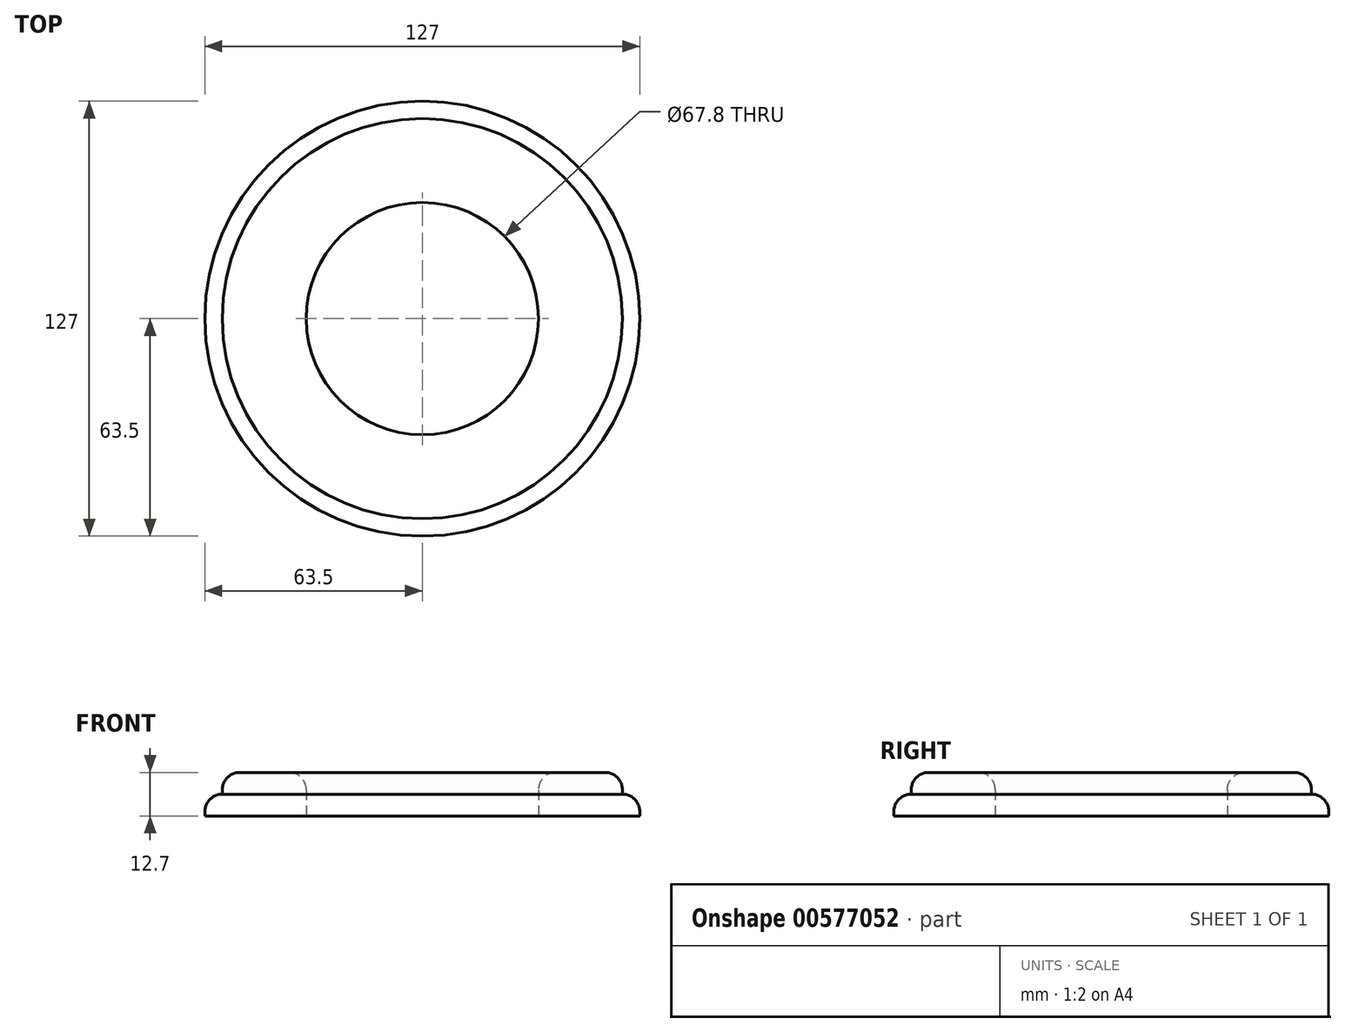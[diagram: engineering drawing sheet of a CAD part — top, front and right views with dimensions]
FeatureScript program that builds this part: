
annotation { "Feature Type Name" : "Feature", "Feature Type Description" : "" }
export const myFeature = defineFeature(function(context is Context, id is Id, definition is map)
    precondition{}
    {
        {
            var Q0;
            Q0=qCreatedBy(makeId("Top.planeOp"),FACE);
            var sketch = newSketch(context, id + "F0", { "sketchPlane" : qUnion([Q0])});
            skCircle(sketch, "E0", {"center": v(0, 0) * mm, "radius": 63.5 * mm});
            skLineSegment(sketch, "E1", {"start": v(-63.5, 0) * mm, "end": v(63.5, 0) * mm});
            skLineSegment(sketch, "E2", {"start": v(63.5, 0) * mm, "end": v(0, 0) * mm});
            skLineSegment(sketch, "E3", {"start": v(0, 63.5) * mm, "end": v(0, -63.5) * mm});
            skCircle(sketch, "E4", {"center": v(0, 0) * mm, "radius": 33.9 * mm});
            skSolve(sketch);
        }
        {
            var Q0;
            Q0 = qSketchRegion(id + "F0", true);
            extrude(context, id + "F1", {"entities" : qUnion([Q0]), "depth" : 6.35 * mm, "offsetDistance" : 25.4 * mm});
        }
        {
            var Q0;
            Q0=makeQuery(id+"F1.opExtrude","CAP_EDGE",EDGE,{"disambiguationData":[OSD([sQuery(id+"F0.wireOp",EDGE,"E0")])],"isStart":false});
            fillet(context, id + "F2", {"entities" : qUnion([Q0]), "radius" : 5.08 * mm, "tangentPropagation" : true, "allowEdgeOverflow" : false});
        }
        {
            var Q0;
            Q0=makeQuery(id+"F1.opExtrude","CAP_FACE",FACE,{"disambiguationData":[OSD([sQuery(id+"F0.wireOp",EDGE,"E0")])],"isStart":false});
            extrude(context, id + "F3", {"entities" : qUnion([Q0]), "operationType" : NewBodyOperationType.ADD, "depth" : 6.35 * mm, "offsetDistance" : 25.4 * mm});
        }
        {
            var Q0;
            Q0=makeQuery(id+"F3.opExtrude","CAP_FACE",FACE,{"disambiguationData":[OSD([sQuery(id+"F0.wireOp",EDGE,"E0")])],"isStart":false});
            fillet(context, id + "F4", {"entities" : qUnion([Q0]), "radius" : 5.08 * mm, "tangentPropagation" : true, "allowEdgeOverflow" : false});
        }
    });
